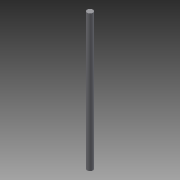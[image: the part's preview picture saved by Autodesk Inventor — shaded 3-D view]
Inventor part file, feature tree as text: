
AUTODESK INVENTOR PART (.ipt)
format: ipt  version: 2015 (Build 190159000, 159)  size: 62,976 bytes
history: native  units: in
note: dims shown in document units (in); Inventor stores cm internally (conversion verified against a paired STEP export)
features: extrude x1, sketch x1
ambient origin geometry x8: Origin, YZ Plane, XZ Plane, XY Plane, X Axis, Y Axis, Z Axis, Center Point
bodies: Solid1 (feature_tree)
feature tree (2):
  extrude  "Extrusion1"  Depth=3.0in TaperAngle=0.0deg
  sketch  "Sketch1"  dims[d0=0.125in d1=3.0in d2=0.0in]
